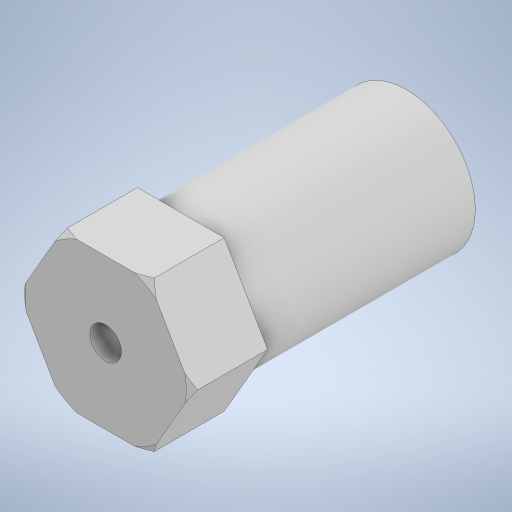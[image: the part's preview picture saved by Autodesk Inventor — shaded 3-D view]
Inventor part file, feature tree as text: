
AUTODESK INVENTOR PART (.ipt)
format: ipt  version: 2024 (Build 280153000, 153)  size: 434,176 bytes
history: native  units: mm
features: sketch x4, extrude x3, revolve x1, chamfer x1
ambient origin geometry x8: Origin, YZ Plane, XZ Plane, XY Plane, X Axis, Y Axis, Z Axis, Center Point
bodies: Body1 (feature_tree)
feature tree (9):
  extrude  "Extrusion6"  Depth=6.0mm TaperAngle=0.0deg
  extrude  "Extrusion7"  Depth=5.1mm
  revolve  "Revolution1"  [1 undecoded]
  chamfer  "Chamfer3"  Distance=18.0mm
  extrude  "Extrusion8"  Depth=6.981317mm
  sketch  "Sketch7"  dims[d24=12.0mm d25=6.0mm d26=0.0mm]
  sketch  "Sketch8"  dims[d27=11.0mm d28=5.1mm]
  sketch  "Sketch9"  dims[d29=4.5mm d30=1.573213mm d31=18.0mm d32=0.0mm]
  sketch  "Sketch10"  dims[d33=0.5mm d35=6.981317mm d38=90.0deg d39=0.125mm d40=0.104887mm d41=1.0mm d42=2.0mm d43=45.0deg d44=2.5mm d45=0.0mm d46=0.0mm]
note: 1 required parameter value undecoded (feature->parameter linkage not recoverable at this tier; creation-order binding heuristic only, values carry confidence <= 0.55)
